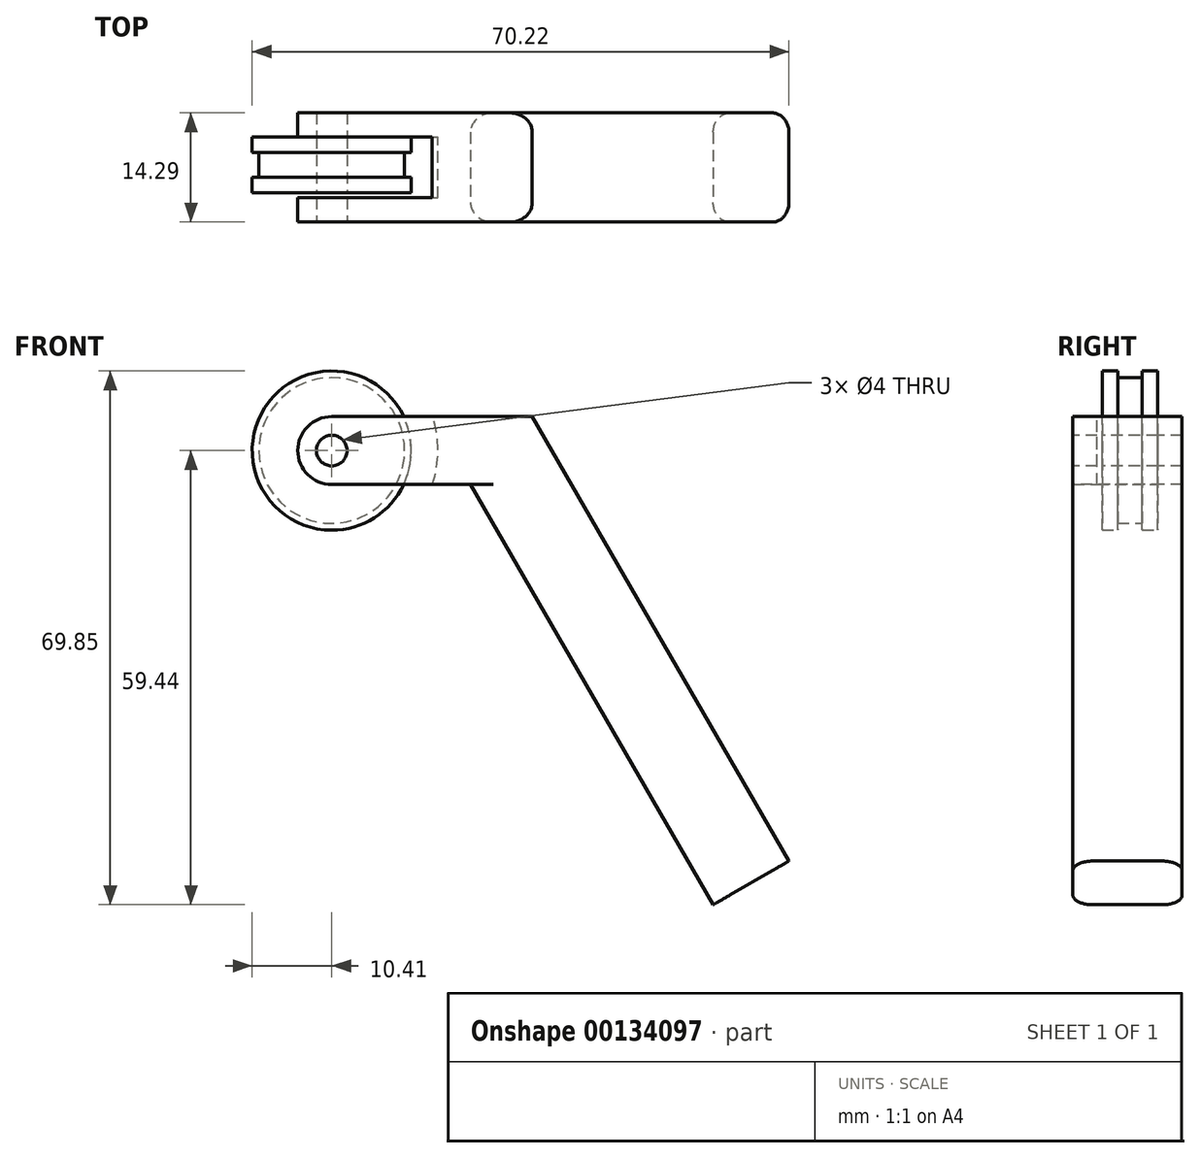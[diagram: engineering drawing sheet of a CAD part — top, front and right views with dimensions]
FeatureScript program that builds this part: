
annotation { "Feature Type Name" : "Feature", "Feature Type Description" : "" }
export const myFeature = defineFeature(function(context is Context, id is Id, definition is map)
    precondition{}
    {
        {
            var Q0;
            Q0=qCreatedBy(makeId("Front.planeOp"),FACE);
            var sketch = newSketch(context, id + "F0", { "sketchPlane" : qUnion([Q0])});
            skCircle(sketch, "E0", {"center": v(0, 0) * mm, "radius": 10.41 * mm});
            skSolve(sketch);
        }
        {
            var Q0;
            Q0=makeQuery(id+"F0.imprint","IMPRINT",FACE,{"disambiguationData":[TD([[makeQuery(id+"F0.imprint","IMPRINT",EDGE,{"derivedFrom":sQuery(id+"F0.wireOp",EDGE,"E0")}),1.0]])]});
            extrude(context, id + "F1", {"entities" : qUnion([Q0]), "depth" : 2.03 * mm});
        }
        {
            var Q0;
            Q0=makeQuery(id+"F1.opExtrude","CAP_FACE",FACE,{"disambiguationData":[OSD([sQuery(id+"F0.wireOp",EDGE,"E0")])],"isStart":false});
            var sketch = newSketch(context, id + "F2", { "sketchPlane" : qUnion([Q0])});
            skCircle(sketch, "E1", {"center": v(0, 0) * mm, "radius": 9.53 * mm});
            skSolve(sketch);
        }
        {
            var Q0;
            Q0 = qSketchRegion(id + "F2", true);
            extrude(context, id + "F3", {"entities" : qUnion([Q0]), "operationType" : NewBodyOperationType.ADD, "depth" : 3.23 * mm});
        }
        {
            var Q0;
            Q0=makeQuery(id+"F3.opExtrude","CAP_FACE",FACE,{"disambiguationData":[OSD([sQuery(id+"F2.wireOp",EDGE,"E1")])],"isStart":false});
            var sketch = newSketch(context, id + "F4", { "sketchPlane" : qUnion([Q0])});
            skCircle(sketch, "E2", {"center": v(0, 0) * mm, "radius": 10.41 * mm});
            skSolve(sketch);
        }
        {
            var Q0;
            Q0 = qSketchRegion(id + "F4", true);
            extrude(context, id + "F5", {"entities" : qUnion([Q0]), "operationType" : NewBodyOperationType.ADD, "depth" : 2.03 * mm});
        }
        {
            var Q0;
            Q0=makeQuery(id+"F5.opExtrude","CAP_FACE",FACE,{"disambiguationData":[OSD([sQuery(id+"F4.wireOp",EDGE,"E2")])],"isStart":false});
            var sketch = newSketch(context, id + "F6", { "sketchPlane" : qUnion([Q0])});
            skCircle(sketch, "E3", {"center": v(0, 0) * mm, "radius": 2 * mm});
            skSolve(sketch);
        }
        {
            var Q0;
            Q0 = qSketchRegion(id + "F6", true);
            extrude(context, id + "F7", {"entities" : qUnion([Q0]), "operationType" : NewBodyOperationType.REMOVE, "endBound" : BoundingType.THROUGH_ALL, "oppositeDirection" : true, "depth" : 25.4 * mm});
        }
        {
            var Q0;
            Q0=makeQuery(id+"F1.opExtrude","CAP_FACE",FACE,{"disambiguationData":[OSD([sQuery(id+"F0.wireOp",EDGE,"E0")])],"isStart":true});
            var sketch = newSketch(context, id + "F8", { "sketchPlane" : qUnion([Q0])});
            skArc(sketch, "E4", {"start": v(0, -4.45) * mm, "mid": v(4.45, 0) * mm, "end": v(0, 4.45) * mm});
            skLineSegment(sketch, "E5", {"start": v(0, 4.45) * mm, "end": v(-26.23, 4.45) * mm});
            skLineSegment(sketch, "E6", {"start": v(-18.16, -4.45) * mm, "end": v(0, -4.45) * mm});
            skLineSegment(sketch, "E7", {"start": v(-18.16, -4.45) * mm, "end": v(-49.91, -59.44) * mm});
            skLineSegment(sketch, "E8", {"start": v(-49.91, -59.44) * mm, "end": v(-59.81, -53.72) * mm});
            skLineSegment(sketch, "E9", {"start": v(-59.81, -53.72) * mm, "end": v(-26.23, 4.44) * mm});
            skSolve(sketch);
        }
        {
            var Q0;
            Q0 = qSketchRegion(id + "F8", true);
            extrude(context, id + "F9", {"entities" : qUnion([Q0]), "depth" : 3.17 * mm});
        }
        {
            var Q0;
            Q0=makeQuery(id+"F9.opExtrude","CAP_FACE",FACE,{"disambiguationData":[OSD([sQuery(id+"F8.wireOp",EDGE,"E4"),sQuery(id+"F8.wireOp",EDGE,"E5"),sQuery(id+"F8.wireOp",EDGE,"E6"),sQuery(id+"F8.wireOp",EDGE,"E7"),sQuery(id+"F8.wireOp",EDGE,"E8"),sQuery(id+"F8.wireOp",EDGE,"E9")])],"isStart":true});
            var sketch = newSketch(context, id + "F10", { "sketchPlane" : qUnion([Q0])});
            skLineSegment(sketch, "E10.0", {"start": v(13.16, 4.45) * mm, "end": v(26.23, 4.45) * mm});
            skLineSegment(sketch, "E10.1", {"start": v(59.81, -53.72) * mm, "end": v(26.23, 4.44) * mm});
            skLineSegment(sketch, "E10.2", {"start": v(49.91, -59.44) * mm, "end": v(59.81, -53.72) * mm});
            skLineSegment(sketch, "E10.3", {"start": v(18.16, -4.45) * mm, "end": v(49.91, -59.44) * mm});
            skLineSegment(sketch, "E10.4", {"start": v(18.16, -4.45) * mm, "end": v(13.16, -4.45) * mm});
            skPoint(sketch, "E11.orphan", {"position": v(0, 4.45) * mm});
            skPoint(sketch, "E12.orphan", {"position": v(0, -4.45) * mm});
            skArc(sketch, "E13", {"start": v(13.16, -4.45) * mm, "mid": v(13.9, 0) * mm, "end": v(13.16, 4.45) * mm});
            skSolve(sketch);
        }
        {
            var Q0;
            Q0=makeQuery(id+"F10.imprint","IMPRINT",FACE,{"disambiguationData":[TD([[makeQuery(id+"F10.imprint","IMPRINT",EDGE,{"derivedFrom":sQuery(id+"F10.wireOp",EDGE,"E10.0")}),-1.0]])]});
            extrude(context, id + "F11", {"entities" : qUnion([Q0]), "operationType" : NewBodyOperationType.ADD, "depth" : 7.94 * mm});
        }
        {
            var Q0;
            Q0=makeQuery(id+"F11.opExtrude","CAP_FACE",FACE,{"disambiguationData":[OSD([sQuery(id+"F10.wireOp",EDGE,"E10.0"),sQuery(id+"F10.wireOp",EDGE,"E10.1"),sQuery(id+"F10.wireOp",EDGE,"E10.2"),sQuery(id+"F10.wireOp",EDGE,"E10.3"),sQuery(id+"F10.wireOp",EDGE,"E10.4"),sQuery(id+"F10.wireOp",EDGE,"E13")])],"isStart":false});
            var sketch = newSketch(context, id + "F12", { "sketchPlane" : qUnion([Q0])});
            skLineSegment(sketch, "E14.6.0", {"start": v(18.16, -4.45) * mm, "end": v(0, -4.45) * mm});
            skArc(sketch, "E14.6.1", {"start": v(0, -4.45) * mm, "mid": v(-4.45, 0) * mm, "end": v(0, 4.45) * mm});
            skLineSegment(sketch, "E14.6.2", {"start": v(0, 4.45) * mm, "end": v(26.23, 4.45) * mm});
            skLineSegment(sketch, "E14.6.3", {"start": v(26.23, 4.44) * mm, "end": v(59.81, -53.72) * mm});
            skLineSegment(sketch, "E14.6.4", {"start": v(59.81, -53.72) * mm, "end": v(49.91, -59.44) * mm});
            skLineSegment(sketch, "E14.6.5", {"start": v(49.91, -59.44) * mm, "end": v(18.16, -4.45) * mm});
            skSolve(sketch);
        }
        {
            var Q0;
            Q0 = qSketchRegion(id + "F12", true);
            extrude(context, id + "F13", {"entities" : qUnion([Q0]), "operationType" : NewBodyOperationType.ADD, "depth" : 3.17 * mm});
        }
        {
            var Q0;
            Q0=makeQuery(id+"F13.opExtrude","CAP_EDGE",EDGE,{"disambiguationData":[OSD([sQuery(id+"F12.wireOp",EDGE,"E14.6.3")])],"isStart":false});
            var Q1;
            Q1=makeQuery(id+"F13.opExtrude","CAP_EDGE",EDGE,{"disambiguationData":[OSD([sQuery(id+"F12.wireOp",EDGE,"E14.6.5")])],"isStart":false});
            var Q2;
            Q2=makeQuery(id+"F9.opExtrude","CAP_EDGE",EDGE,{"disambiguationData":[OSD([sQuery(id+"F8.wireOp",EDGE,"E9")])],"isStart":false});
            var Q3;
            Q3=makeQuery(id+"F9.opExtrude","CAP_EDGE",EDGE,{"disambiguationData":[OSD([sQuery(id+"F8.wireOp",EDGE,"E7")])],"isStart":false});
            fillet(context, id + "F14", {"entities" : qUnion([Q0, Q1, Q2, Q3]), "radius" : 2.54 * mm, "tangentPropagation" : true, "allowEdgeOverflow" : false});
        }
        {
            var Q0;
            Q0=makeQuery(id+"F13.opExtrude","CAP_FACE",FACE,{"disambiguationData":[OSD([sQuery(id+"F12.wireOp",EDGE,"E14.6.0"),sQuery(id+"F12.wireOp",EDGE,"E14.6.1"),sQuery(id+"F12.wireOp",EDGE,"E14.6.2"),sQuery(id+"F12.wireOp",EDGE,"E14.6.3"),sQuery(id+"F12.wireOp",EDGE,"E14.6.4"),sQuery(id+"F12.wireOp",EDGE,"E14.6.5")])],"isStart":false});
            var sketch = newSketch(context, id + "F15", { "sketchPlane" : qUnion([Q0])});
            skCircle(sketch, "E15", {"center": v(0, 0) * mm, "radius": 2 * mm});
            skSolve(sketch);
        }
        {
            var Q0;
            Q0 = qSketchRegion(id + "F15", true);
            extrude(context, id + "F16", {"entities" : qUnion([Q0]), "operationType" : NewBodyOperationType.REMOVE, "endBound" : BoundingType.THROUGH_ALL, "oppositeDirection" : true, "depth" : 25.4 * mm});
        }
    });
